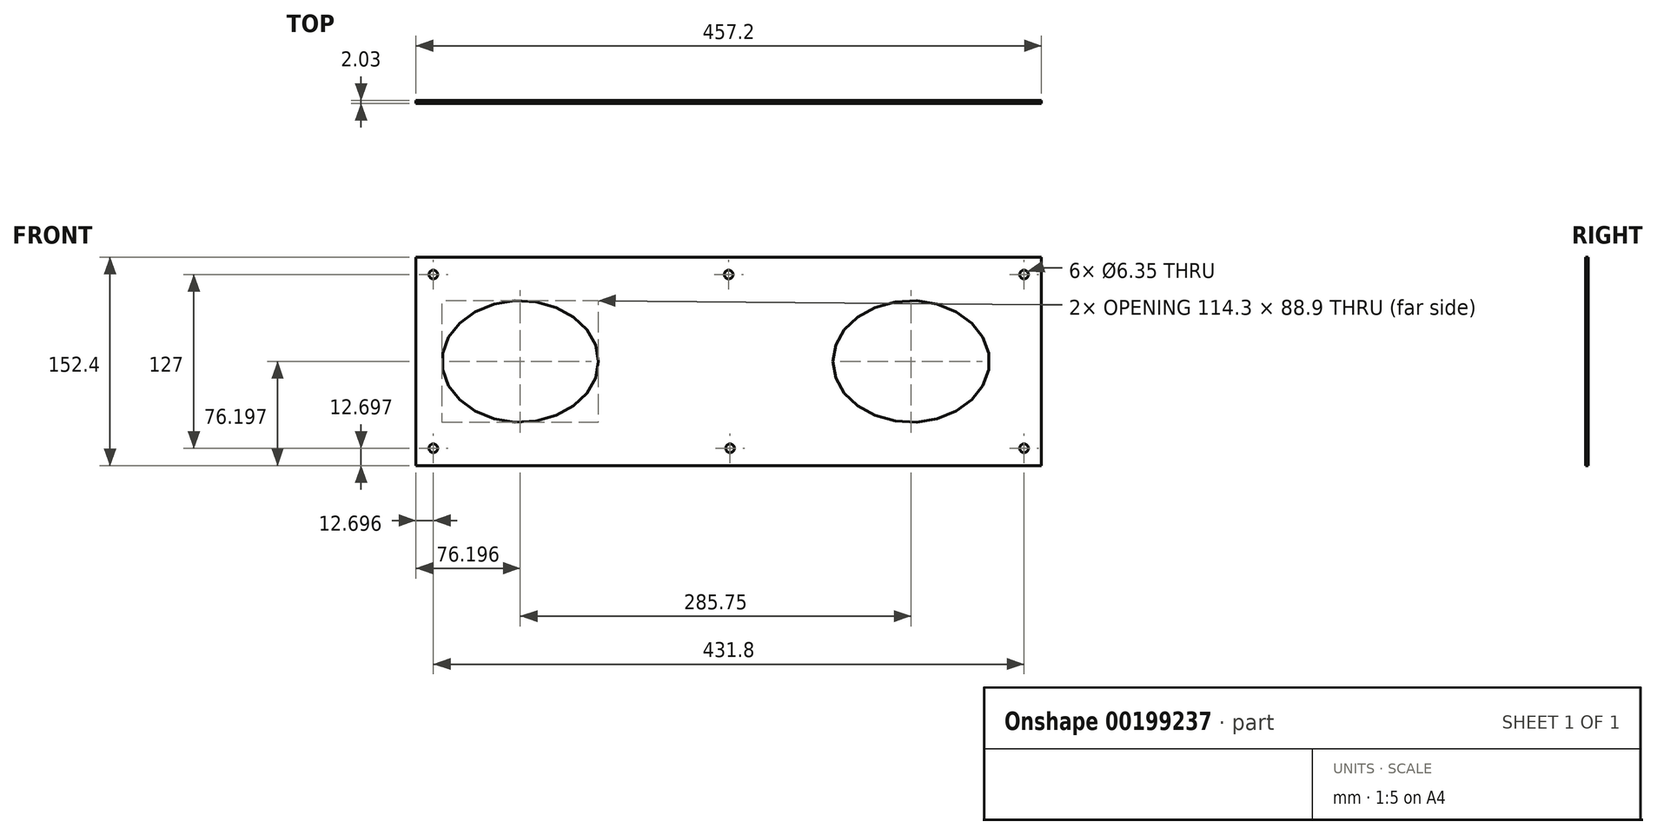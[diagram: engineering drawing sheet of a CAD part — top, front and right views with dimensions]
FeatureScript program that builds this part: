
annotation { "Feature Type Name" : "Feature", "Feature Type Description" : "" }
export const myFeature = defineFeature(function(context is Context, id is Id, definition is map)
    precondition{}
    {
        {
            var Q0;
            Q0=qCreatedBy(makeId("Front.planeOp"),FACE);
            var sketch = newSketch(context, id + "F0", { "sketchPlane" : qUnion([Q0])});
            skLineSegment(sketch, "E0.bottom", {"start": v(-335.11, 118.13) * mm, "end": v(122.09, 118.13) * mm});
            skLineSegment(sketch, "E0.top", {"start": v(-335.11, -34.27) * mm, "end": v(122.09, -34.27) * mm});
            skLineSegment(sketch, "E0.left", {"start": v(-335.11, 118.13) * mm, "end": v(-335.11, -34.27) * mm});
            skLineSegment(sketch, "E0.right", {"start": v(122.09, 118.13) * mm, "end": v(122.09, -34.27) * mm});
            skPoint(sketch, "E1", {"position": v(-258.91, 41.93) * mm});
            skPoint(sketch, "E2", {"position": v(26.84, 41.93) * mm});
            skEllipse(sketch, "E3", {"center": v(-258.91, 41.93) * mm, "majorRadius": 57.15 * mm, "minorRadius": 44.45 * mm, "majorAxis": v(1, 0)});
            skEllipse(sketch, "E4", {"center": v(26.84, 41.93) * mm, "majorRadius": 57.15 * mm, "minorRadius": 44.45 * mm, "majorAxis": v(-1, 0)});
            skPoint(sketch, "E5", {"position": v(-322.41, 105.43) * mm});
            skPoint(sketch, "E6", {"position": v(-106.51, 105.43) * mm});
            skPoint(sketch, "E6.positionSnap0", {"position": v(-106.51, 118.13) * mm});
            skPoint(sketch, "E7", {"position": v(109.39, 105.43) * mm});
            skPoint(sketch, "E8", {"position": v(109.39, -21.57) * mm});
            skPoint(sketch, "E9", {"position": v(-105.52, -21.57) * mm});
            skPoint(sketch, "E10", {"position": v(-322.41, -21.57) * mm});
            skCircle(sketch, "E11", {"center": v(-322.41, 105.43) * mm, "radius": 3.18 * mm});
            skCircle(sketch, "E12", {"center": v(-322.41, -21.57) * mm, "radius": 3.18 * mm});
            skCircle(sketch, "E13", {"center": v(-106.51, 105.43) * mm, "radius": 3.18 * mm});
            skCircle(sketch, "E14", {"center": v(109.39, 105.43) * mm, "radius": 3.18 * mm});
            skCircle(sketch, "E15", {"center": v(-105.52, -21.57) * mm, "radius": 3.18 * mm});
            skCircle(sketch, "E16", {"center": v(109.39, -21.57) * mm, "radius": 3.18 * mm});
            skSolve(sketch);
        }
        {
            var Q0;
            Q0 = qSketchRegion(id + "F0", true);
            extrude(context, id + "F1", {"entities" : qUnion([Q0]), "oppositeDirection" : true, "depth" : 2.03 * mm});
        }
    });
